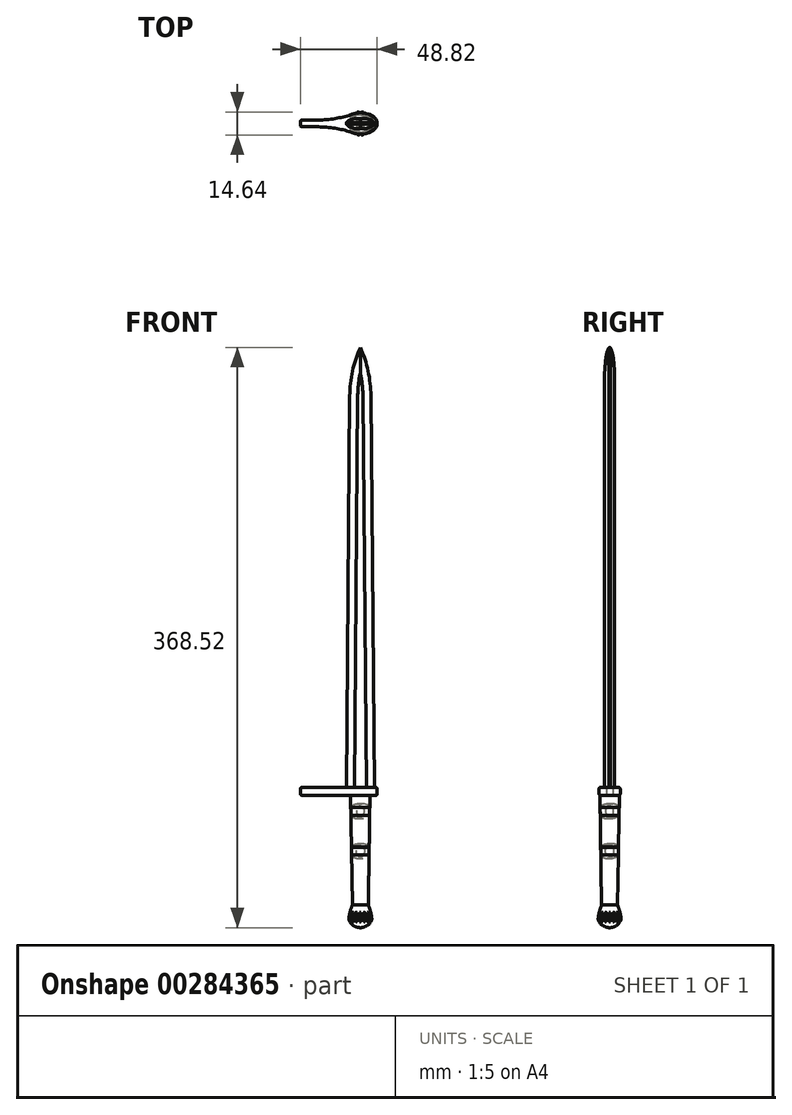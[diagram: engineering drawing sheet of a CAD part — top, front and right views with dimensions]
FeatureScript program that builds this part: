
annotation { "Feature Type Name" : "Feature", "Feature Type Description" : "" }
export const myFeature = defineFeature(function(context is Context, id is Id, definition is map)
    precondition{}
    {
        {
            var Q0;
            Q0=qCreatedBy(makeId("Right.planeOp"),FACE);
            var sketch = newSketch(context, id + "F0", { "sketchPlane" : qUnion([Q0])});
            skLineSegment(sketch, "E0", {"start": v(0, 0) * mm, "end": v(-6.1, 0) * mm});
            skLineSegment(sketch, "E1", {"start": v(0, 0) * mm, "end": v(0, -52.88) * mm});
            skLineSegment(sketch, "E2", {"start": v(0, 0) * mm, "end": v(6.1, 0) * mm});
            skPoint(sketch, "E3.end.orphan", {"position": v(-6.1, 0) * mm});
            skLineSegment(sketch, "E4", {"start": v(0, -52.88) * mm, "end": v(0, -69.72) * mm});
            skLineSegment(sketch, "E5", {"start": v(0, -69.72) * mm, "end": v(-5.08, -69.72) * mm});
            skLineSegment(sketch, "E6.MirrorCS", {"start": v(0, -69.72) * mm, "end": v(5.08, -69.72) * mm});
            skLineSegment(sketch, "E7", {"start": v(-5.08, -69.72) * mm, "end": v(-6.1, 0) * mm});
            skLineSegment(sketch, "E8", {"start": v(5.08, -69.72) * mm, "end": v(6.1, 0) * mm});
            skArc(sketch, "E9", {"start": v(-5.98, -7.62) * mm, "mid": v(-6.68, -10.11) * mm, "end": v(-5.91, -12.59) * mm});
            skLineSegment(sketch, "E10", {"start": v(-5.58, -35.4) * mm, "end": v(-13.44, -35.51) * mm});
            skArc(sketch, "E11.MirrorCS", {"start": v(-5.18, -63.18) * mm, "mid": v(-5.94, -60.7) * mm, "end": v(-5.25, -58.2) * mm});
            skLineSegment(sketch, "E12", {"start": v(-2.07, -10.05) * mm, "end": v(-5.91, -10.1) * mm});
            skLineSegment(sketch, "E13", {"start": v(-5.75, -22.75) * mm, "end": v(-5.91, -10.1) * mm});
            skPoint(sketch, "E14", {"position": v(-5.75, -22.75) * mm});
            skLineSegment(sketch, "E15", {"start": v(-5.75, -22.75) * mm, "end": v(-9.83, -22.8) * mm});
            skArc(sketch, "E16.MirrorCS", {"start": v(-5.59, -37.88) * mm, "mid": v(-6.34, -35.4) * mm, "end": v(-5.65, -32.91) * mm});
            skLineSegment(sketch, "E17", {"start": v(-5.59, -37.88) * mm, "end": v(-5.54, -37.95) * mm});
            skLineSegment(sketch, "E18", {"start": v(-5.65, -32.91) * mm, "end": v(-5.62, -32.87) * mm});
            skSolve(sketch);
        }
        {
            var Q0;
            {var subQ8=sQuery(id+"F0.wireOp",EDGE,"E0");Q0=makeQuery(id+"F0.imprint","IMPRINT",FACE,{"disambiguationData":[TD([[makeQuery(id+"F0.imprint","IMPRINT",EDGE,{"derivedFrom":subQ8}),1.0]])]});}
            var Q1;
            Q1=sQuery(id+"F0.wireOp",EDGE,"E1");
            revolve(context, id + "F1", {"entities" : qUnion([Q0]), "axis" : qUnion([Q1]), "revolveType" : RevolveType.FULL});
        }
        {
            var Q0;
            {var subQ3=sQuery(id+"F0.wireOp",EDGE,"E18");Q0=makeQuery(id+"F0.imprint","IMPRINT",FACE,{"disambiguationData":[TD([[makeQuery(id+"F0.imprint","IMPRINT",EDGE,{"derivedFrom":subQ3}),-1.0]])]});}
            var Q1;
            {var subQ3=sQuery(id+"F0.wireOp",EDGE,"E17");Q1=makeQuery(id+"F0.imprint","IMPRINT",FACE,{"disambiguationData":[TD([[makeQuery(id+"F0.imprint","IMPRINT",EDGE,{"derivedFrom":subQ3}),1.0]])]});}
            var Q2;
            {var subQ0=sQuery(id+"F0.wireOp",EDGE,"E9");Q2=makeQuery(id+"F0.imprint","IMPRINT",FACE,{"disambiguationData":[TD([[makeQuery(id+"F0.imprint","IMPRINT",EDGE,{"derivedFrom":subQ0}),1.0]])]});}
            var Q3;
            {var subQ0=sQuery(id+"F0.wireOp",EDGE,"E11.MirrorCS");Q3=makeQuery(id+"F0.imprint","IMPRINT",FACE,{"disambiguationData":[TD([[makeQuery(id+"F0.imprint","IMPRINT",EDGE,{"derivedFrom":subQ0}),-1.0]])]});}
            var Q4;
            Q4=sQuery(id+"F0.wireOp",EDGE,"E4");
            revolve(context, id + "F2", {"entities" : qUnion([Q0, Q1, Q2, Q3]), "axis" : qUnion([Q4]), "revolveType" : RevolveType.FULL});
        }
        {
            var Q0;
            Q0=makeQuery(id+"F1.opRevolve","SWEPT_FACE",FACE,{"disambiguationData":[OSD([sQuery(id+"F0.wireOp",EDGE,"E0")])]});
            var sketch = newSketch(context, id + "F3", { "sketchPlane" : qUnion([Q0])});
            skEllipse(sketch, "E19", {"center": v(0, 0) * mm, "majorRadius": 6.74 * mm, "minorRadius": 10.7 * mm, "majorAxis": v(0, 1)});
            skLineSegment(sketch, "E20", {"start": v(-10.7, 0) * mm, "end": v(-38.12, 0) * mm});
            skPoint(sketch, "E20.endSnap0", {"position": v(-10.7, 0) * mm});
            skLineSegment(sketch, "E21", {"start": v(-38.12, 0) * mm, "end": v(-38.12, 2.16) * mm});
            skLineSegment(sketch, "E22", {"start": v(-38.12, 2.16) * mm, "end": v(-27.96, 2.16) * mm});
            skArc(sketch, "E23", {"start": v(-27.96, 2.16) * mm, "mid": v(-17.38, 2.9) * mm, "end": v(-7, 5.1) * mm});
            skArc(sketch, "E24.MirrorCS", {"start": v(-27.96, -2.16) * mm, "mid": v(-17.38, -2.9) * mm, "end": v(-7, -5.1) * mm});
            skLineSegment(sketch, "E25.MirrorCS", {"start": v(-38.12, -2.16) * mm, "end": v(-27.96, -2.16) * mm});
            skLineSegment(sketch, "E26.MirrorCS", {"start": v(-38.12, 0) * mm, "end": v(-38.12, -2.16) * mm});
            skLineSegment(sketch, "E27", {"start": v(0, 0) * mm, "end": v(0, 3.03) * mm});
            skArc(sketch, "E28.MirrorCS", {"start": v(27.96, 2.16) * mm, "mid": v(17.38, 2.9) * mm, "end": v(7, 5.1) * mm});
            skArc(sketch, "E29.MirrorCS", {"start": v(27.96, -2.16) * mm, "mid": v(17.38, -2.9) * mm, "end": v(7, -5.1) * mm});
            skLineSegment(sketch, "E30.MirrorCS", {"start": v(38.12, 0) * mm, "end": v(38.12, -2.16) * mm});
            skLineSegment(sketch, "E31.MirrorCS", {"start": v(38.12, 0) * mm, "end": v(38.12, 2.16) * mm});
            skLineSegment(sketch, "E32.MirrorCS", {"start": v(38.12, 2.16) * mm, "end": v(27.96, 2.16) * mm});
            skLineSegment(sketch, "E33.MirrorCS", {"start": v(38.12, -2.16) * mm, "end": v(27.96, -2.16) * mm});
            skSolve(sketch);
        }
        {
            var Q0;
            {var subQ1=sQuery(id+"F3.wireOp",EDGE,"E20");Q0=makeQuery(id+"F3.imprint","IMPRINT",FACE,{"disambiguationData":[TD([[makeQuery(id+"F3.imprint","IMPRINT",EDGE,{"derivedFrom":subQ1}),-1.0]])]});}
            var Q1;
            {var subQ1=sQuery(id+"F3.wireOp",EDGE,"E20");Q1=makeQuery(id+"F3.imprint","IMPRINT",FACE,{"disambiguationData":[TD([[makeQuery(id+"F3.imprint","IMPRINT",EDGE,{"derivedFrom":subQ1}),1.0]])]});}
            var Q2;
            Q2=makeQuery(id+"F3.imprint","IMPRINT",FACE,{"disambiguationData":[TD([[makeQuery(id+"F3.imprint","IMPRINT",EDGE,{"derivedFrom":makeQuery(id+"F1.opRevolve","SWEPT_EDGE",EDGE,{"disambiguationData":[OSD([sQuery(id+"F0.wireOp",EDGE,"E0"),sQuery(id+"F0.wireOp",EDGE,"E7")])]})}),-1.0]])]});
            var Q3;
            {var subQ0=sQuery(id+"F3.wireOp",EDGE,"E28.MirrorCS");Q3=makeQuery(id+"F3.imprint","IMPRINT",FACE,{"disambiguationData":[TD([[makeQuery(id+"F3.imprint","IMPRINT",EDGE,{"derivedFrom":subQ0}),1.0]])]});}
            var Q4;
            Q4=makeQuery(id+"F3.imprint","IMPRINT",FACE,{"disambiguationData":[TD([[makeQuery(id+"F3.imprint","IMPRINT",EDGE,{"derivedFrom":makeQuery(id+"F1.opRevolve","SWEPT_EDGE",EDGE,{"disambiguationData":[OSD([sQuery(id+"F0.wireOp",EDGE,"E0"),sQuery(id+"F0.wireOp",EDGE,"E7")])]})}),1.0]])]});
            extrude(context, id + "F4", {"entities" : qUnion([Q0, Q1, Q2, Q3, Q4]), "depth" : 5.08 * mm});
        }
        {
            var Q0;
            Q0=makeQuery(id+"F4.opExtrude","CAP_EDGE",EDGE,{"disambiguationData":[OSD([sQuery(id+"F3.wireOp",EDGE,"E24.MirrorCS")])],"isStart":false});
            var Q1;
            Q1=makeQuery(id+"F4.opExtrude","CAP_EDGE",EDGE,{"disambiguationData":[OSD([sQuery(id+"F3.wireOp",EDGE,"E25.MirrorCS")])],"isStart":false});
            var Q2;
            Q2=makeQuery(id+"F4.opExtrude","CAP_EDGE",EDGE,{"disambiguationData":[OSD([sQuery(id+"F3.wireOp",EDGE,"E25.MirrorCS")])],"isStart":true});
            var Q3;
            Q3=makeQuery(id+"F4.opExtrude","CAP_EDGE",EDGE,{"disambiguationData":[OSD([sQuery(id+"F3.wireOp",EDGE,"E24.MirrorCS")])],"isStart":true});
            var Q4;
            Q4=makeQuery(id+"F4.opExtrude","CAP_EDGE",EDGE,{"disambiguationData":[OSD([sQuery(id+"F3.wireOp",EDGE,"E23")])],"isStart":true});
            var Q5;
            Q5=makeQuery(id+"F4.opExtrude","CAP_EDGE",EDGE,{"disambiguationData":[OSD([sQuery(id+"F3.wireOp",EDGE,"E23")])],"isStart":false});
            var Q6;
            Q6=makeQuery(id+"F4.opExtrude","CAP_EDGE",EDGE,{"disambiguationData":[OSD([sQuery(id+"F3.wireOp",EDGE,"E22")])],"isStart":false});
            var Q7;
            Q7=makeQuery(id+"F4.opExtrude","SWEPT_EDGE",EDGE,{"disambiguationData":[OSD([sQuery(id+"F3.wireOp",EDGE,"E25.MirrorCS"),sQuery(id+"F3.wireOp",EDGE,"E26.MirrorCS")])]});
            var Q8;
            Q8=makeQuery(id+"F4.opExtrude","SWEPT_EDGE",EDGE,{"disambiguationData":[OSD([sQuery(id+"F3.wireOp",EDGE,"E21"),sQuery(id+"F3.wireOp",EDGE,"E22")])]});
            var Q9;
            Q9=makeQuery(id+"F4.opExtrude","CAP_EDGE",EDGE,{"disambiguationData":[OSD([sQuery(id+"F3.wireOp",EDGE,"E21"),sQuery(id+"F3.wireOp",EDGE,"E26.MirrorCS")])],"isStart":true});
            var Q10;
            Q10=makeQuery(id+"F4.opExtrude","CAP_EDGE",EDGE,{"disambiguationData":[OSD([sQuery(id+"F3.wireOp",EDGE,"E21"),sQuery(id+"F3.wireOp",EDGE,"E26.MirrorCS")])],"isStart":false});
            var Q11;
            Q11=makeQuery(id+"F4.opExtrude","CAP_EDGE",EDGE,{"disambiguationData":[OSD([sQuery(id+"F3.wireOp",EDGE,"E29.MirrorCS")])],"isStart":false});
            var Q12;
            Q12=makeQuery(id+"F4.opExtrude","CAP_EDGE",EDGE,{"disambiguationData":[OSD([sQuery(id+"F3.wireOp",EDGE,"E29.MirrorCS")])],"isStart":true});
            var Q13;
            Q13=makeQuery(id+"F4.opExtrude","CAP_EDGE",EDGE,{"disambiguationData":[OSD([sQuery(id+"F3.wireOp",EDGE,"E28.MirrorCS")])],"isStart":false});
            var Q14;
            Q14=makeQuery(id+"F4.opExtrude","CAP_EDGE",EDGE,{"disambiguationData":[OSD([sQuery(id+"F3.wireOp",EDGE,"E28.MirrorCS")])],"isStart":true});
            var Q15;
            Q15=makeQuery(id+"F4.opExtrude","SWEPT_FACE",FACE,{"disambiguationData":[OSD([sQuery(id+"F3.wireOp",EDGE,"E30.MirrorCS"),sQuery(id+"F3.wireOp",EDGE,"E31.MirrorCS")])]});
            var Q16;
            {var subQ0=sQuery(id+"F3.wireOp",EDGE,"E19");Q16=makeQuery(id+"F4.opExtrude","SWEPT_FACE",FACE,{"disambiguationData":[OSD([subQ0]),TDD([makeQuery(id+"F3.imprint","IMPRINT",EDGE,{"disambiguationData":[TD([[makeQuery(id+"F3.imprint","INTERSECT",VERTEX,{"derivedFrom":[subQ0,sQuery(id+"F3.wireOp",EDGE,"E24.MirrorCS")]}),-1.0]])],"derivedFrom":subQ0})])]});}
            var Q17;
            {var subQ0=sQuery(id+"F3.wireOp",EDGE,"E19");Q17=makeQuery(id+"F4.opExtrude","SWEPT_FACE",FACE,{"disambiguationData":[OSD([subQ0]),TDD([makeQuery(id+"F3.imprint","IMPRINT",EDGE,{"disambiguationData":[TD([[makeQuery(id+"F3.imprint","INTERSECT",VERTEX,{"derivedFrom":[subQ0,sQuery(id+"F3.wireOp",EDGE,"E23")]}),1.0]])],"derivedFrom":subQ0})])]});}
            fillet(context, id + "F5", {"entities" : qUnion([Q0, Q1, Q2, Q3, Q4, Q5, Q6, Q7, Q8, Q9, Q10, Q11, Q12, Q13, Q14, Q15, Q16, Q17]), "radius" : 1.02 * mm, "tangentPropagation" : true, "allowEdgeOverflow" : false});
        }
        {
            var Q0;
            Q0=qCreatedBy(makeId("Front.planeOp"),FACE);
            var sketch = newSketch(context, id + "F6", { "sketchPlane" : qUnion([Q0])});
            skLineSegment(sketch, "E34.0", {"start": v(-5.08, -69.72) * mm, "end": v(5.08, -69.72) * mm});
            skArc(sketch, "E35", {"start": v(-5.08, -69.72) * mm, "mid": v(-6.56, -74.06) * mm, "end": v(-7.37, -78.58) * mm});
            skLineSegment(sketch, "E36", {"start": v(0, -69.72) * mm, "end": v(0, -75.64) * mm});
            skPoint(sketch, "E36.endSnap0", {"position": v(0, -69.72) * mm});
            skArc(sketch, "E37.MirrorCS", {"start": v(5.08, -69.72) * mm, "mid": v(6.56, -74.06) * mm, "end": v(7.37, -78.58) * mm});
            skArc(sketch, "E38", {"start": v(-7.37, -78.58) * mm, "mid": v(0, -84.04) * mm, "end": v(7.37, -78.58) * mm});
            skLineSegment(sketch, "E39", {"start": v(0, -72.68) * mm, "end": v(0, -84.04) * mm});
            skSolve(sketch);
        }
        {
            var Q0;
            {var subQ1=sQuery(id+"F6.wireOp",EDGE,"E35");Q0=makeQuery(id+"F6.imprint","IMPRINT",FACE,{"disambiguationData":[TD([[makeQuery(id+"F6.imprint","IMPRINT",EDGE,{"derivedFrom":subQ1}),1.0]])]});}
            var Q1;
            Q1=sQuery(id+"F6.wireOp",EDGE,"E39");
            revolve(context, id + "F7", {"entities" : qUnion([Q0]), "axis" : qUnion([Q1]), "revolveType" : RevolveType.FULL});
        }
        {
            var Q0;
            Q0=makeQuery(id+"F7.opRevolve","SWEPT_FACE",FACE,{"disambiguationData":[OSD([sQuery(id+"F6.wireOp",EDGE,"E34.0")])]});
            var sketch = newSketch(context, id + "F8", { "sketchPlane" : qUnion([Q0])});
            skCircle(sketch, "E40.0", {"center": v(0, 0) * mm, "radius": 7.37 * mm});
            skLineSegment(sketch, "E41", {"start": v(-0.9, 7.32) * mm, "end": v(-0.35, 6.6) * mm});
            skLineSegment(sketch, "E42", {"start": v(0, 7.32) * mm, "end": v(0, 7.11) * mm});
            skLineSegment(sketch, "E43.MirrorCS", {"start": v(0.9, 7.32) * mm, "end": v(0.35, 6.6) * mm});
            skLineSegment(sketch, "E44", {"start": v(-0.35, 6.6) * mm, "end": v(0.35, 6.6) * mm});
            skPoint(sketch, "E45.orphan", {"position": v(0.9, 7.32) * mm});
            skLineSegment(sketch, "E46.1.0", {"start": v(-1.97, 7.1) * mm, "end": v(-2.2, 6.23) * mm});
            skLineSegment(sketch, "E46.1.1", {"start": v(-2.85, 5.96) * mm, "end": v(-2.2, 6.23) * mm});
            skLineSegment(sketch, "E46.1.2", {"start": v(-3.63, 6.42) * mm, "end": v(-2.85, 5.96) * mm});
            skLineSegment(sketch, "E46.2.0", {"start": v(-4.54, 5.8) * mm, "end": v(-4.42, 4.92) * mm});
            skLineSegment(sketch, "E46.2.1", {"start": v(-4.92, 4.42) * mm, "end": v(-4.42, 4.92) * mm});
            skLineSegment(sketch, "E46.2.2", {"start": v(-5.8, 4.54) * mm, "end": v(-4.92, 4.42) * mm});
            skLineSegment(sketch, "E46.3.0", {"start": v(-6.42, 3.63) * mm, "end": v(-5.96, 2.85) * mm});
            skLineSegment(sketch, "E46.3.1", {"start": v(-6.23, 2.2) * mm, "end": v(-5.96, 2.85) * mm});
            skLineSegment(sketch, "E46.3.2", {"start": v(-7.1, 1.97) * mm, "end": v(-6.23, 2.2) * mm});
            skLineSegment(sketch, "E46.4.0", {"start": v(-7.32, 0.9) * mm, "end": v(-6.6, 0.35) * mm});
            skLineSegment(sketch, "E46.4.1", {"start": v(-6.6, -0.35) * mm, "end": v(-6.6, 0.35) * mm});
            skLineSegment(sketch, "E46.4.2", {"start": v(-7.32, -0.9) * mm, "end": v(-6.6, -0.35) * mm});
            skLineSegment(sketch, "E46.5.0", {"start": v(-7.1, -1.97) * mm, "end": v(-6.23, -2.2) * mm});
            skLineSegment(sketch, "E46.5.1", {"start": v(-5.96, -2.85) * mm, "end": v(-6.23, -2.2) * mm});
            skLineSegment(sketch, "E46.5.2", {"start": v(-6.42, -3.63) * mm, "end": v(-5.96, -2.85) * mm});
            skLineSegment(sketch, "E46.6.0", {"start": v(-5.8, -4.54) * mm, "end": v(-4.92, -4.42) * mm});
            skLineSegment(sketch, "E46.6.1", {"start": v(-4.42, -4.92) * mm, "end": v(-4.92, -4.42) * mm});
            skLineSegment(sketch, "E46.6.2", {"start": v(-4.54, -5.8) * mm, "end": v(-4.42, -4.92) * mm});
            skLineSegment(sketch, "E46.7.0", {"start": v(-3.63, -6.42) * mm, "end": v(-2.85, -5.96) * mm});
            skLineSegment(sketch, "E46.7.1", {"start": v(-2.2, -6.23) * mm, "end": v(-2.85, -5.96) * mm});
            skLineSegment(sketch, "E46.7.2", {"start": v(-1.97, -7.1) * mm, "end": v(-2.2, -6.23) * mm});
            skLineSegment(sketch, "E46.8.0", {"start": v(-0.9, -7.32) * mm, "end": v(-0.35, -6.6) * mm});
            skLineSegment(sketch, "E46.8.1", {"start": v(0.35, -6.6) * mm, "end": v(-0.35, -6.6) * mm});
            skLineSegment(sketch, "E46.8.2", {"start": v(0.9, -7.32) * mm, "end": v(0.35, -6.6) * mm});
            skLineSegment(sketch, "E46.9.0", {"start": v(1.97, -7.1) * mm, "end": v(2.2, -6.23) * mm});
            skLineSegment(sketch, "E46.9.1", {"start": v(2.85, -5.96) * mm, "end": v(2.2, -6.23) * mm});
            skLineSegment(sketch, "E46.9.2", {"start": v(3.63, -6.42) * mm, "end": v(2.85, -5.96) * mm});
            skLineSegment(sketch, "E46.10.0", {"start": v(4.54, -5.8) * mm, "end": v(4.42, -4.92) * mm});
            skLineSegment(sketch, "E46.10.1", {"start": v(4.92, -4.42) * mm, "end": v(4.42, -4.92) * mm});
            skLineSegment(sketch, "E46.10.2", {"start": v(5.8, -4.54) * mm, "end": v(4.92, -4.42) * mm});
            skLineSegment(sketch, "E46.11.0", {"start": v(6.42, -3.63) * mm, "end": v(5.96, -2.85) * mm});
            skLineSegment(sketch, "E46.11.1", {"start": v(6.23, -2.2) * mm, "end": v(5.96, -2.85) * mm});
            skLineSegment(sketch, "E46.11.2", {"start": v(7.1, -1.97) * mm, "end": v(6.23, -2.2) * mm});
            skLineSegment(sketch, "E46.12.0", {"start": v(7.32, -0.9) * mm, "end": v(6.6, -0.35) * mm});
            skLineSegment(sketch, "E46.12.1", {"start": v(6.6, 0.35) * mm, "end": v(6.6, -0.35) * mm});
            skLineSegment(sketch, "E46.12.2", {"start": v(7.32, 0.9) * mm, "end": v(6.6, 0.35) * mm});
            skLineSegment(sketch, "E46.13.0", {"start": v(7.1, 1.97) * mm, "end": v(6.23, 2.2) * mm});
            skLineSegment(sketch, "E46.13.1", {"start": v(5.96, 2.85) * mm, "end": v(6.23, 2.2) * mm});
            skLineSegment(sketch, "E46.13.2", {"start": v(6.42, 3.63) * mm, "end": v(5.96, 2.85) * mm});
            skLineSegment(sketch, "E46.14.0", {"start": v(5.8, 4.54) * mm, "end": v(4.92, 4.42) * mm});
            skLineSegment(sketch, "E46.14.1", {"start": v(4.42, 4.92) * mm, "end": v(4.92, 4.42) * mm});
            skLineSegment(sketch, "E46.14.2", {"start": v(4.54, 5.8) * mm, "end": v(4.42, 4.92) * mm});
            skLineSegment(sketch, "E46.15.0", {"start": v(3.63, 6.42) * mm, "end": v(2.85, 5.96) * mm});
            skLineSegment(sketch, "E46.15.1", {"start": v(2.2, 6.23) * mm, "end": v(2.85, 5.96) * mm});
            skLineSegment(sketch, "E46.15.2", {"start": v(1.97, 7.1) * mm, "end": v(2.2, 6.23) * mm});
            skSolve(sketch);
        }
        {
            var Q0;
            {var subQ0=sQuery(id+"F8.wireOp",EDGE,"E46.3.0");Q0=makeQuery(id+"F8.imprint","IMPRINT",FACE,{"disambiguationData":[TD([[makeQuery(id+"F8.imprint","IMPRINT",EDGE,{"derivedFrom":subQ0}),-1.0]])]});}
            var Q1;
            {var subQ0=sQuery(id+"F8.wireOp",EDGE,"E46.4.0");Q1=makeQuery(id+"F8.imprint","IMPRINT",FACE,{"disambiguationData":[TD([[makeQuery(id+"F8.imprint","IMPRINT",EDGE,{"derivedFrom":subQ0}),-1.0]])]});}
            var Q2;
            {var subQ0=sQuery(id+"F8.wireOp",EDGE,"E46.5.0");Q2=makeQuery(id+"F8.imprint","IMPRINT",FACE,{"disambiguationData":[TD([[makeQuery(id+"F8.imprint","IMPRINT",EDGE,{"derivedFrom":subQ0}),-1.0]])]});}
            var Q3;
            {var subQ0=sQuery(id+"F8.wireOp",EDGE,"E46.6.0");Q3=makeQuery(id+"F8.imprint","IMPRINT",FACE,{"disambiguationData":[TD([[makeQuery(id+"F8.imprint","IMPRINT",EDGE,{"derivedFrom":subQ0}),-1.0]])]});}
            var Q4;
            {var subQ0=sQuery(id+"F8.wireOp",EDGE,"E46.7.0");Q4=makeQuery(id+"F8.imprint","IMPRINT",FACE,{"disambiguationData":[TD([[makeQuery(id+"F8.imprint","IMPRINT",EDGE,{"derivedFrom":subQ0}),-1.0]])]});}
            var Q5;
            {var subQ0=sQuery(id+"F8.wireOp",EDGE,"E46.8.0");Q5=makeQuery(id+"F8.imprint","IMPRINT",FACE,{"disambiguationData":[TD([[makeQuery(id+"F8.imprint","IMPRINT",EDGE,{"derivedFrom":subQ0}),-1.0]])]});}
            var Q6;
            {var subQ0=sQuery(id+"F8.wireOp",EDGE,"E46.9.0");Q6=makeQuery(id+"F8.imprint","IMPRINT",FACE,{"disambiguationData":[TD([[makeQuery(id+"F8.imprint","IMPRINT",EDGE,{"derivedFrom":subQ0}),-1.0]])]});}
            var Q7;
            {var subQ0=sQuery(id+"F8.wireOp",EDGE,"E46.10.0");Q7=makeQuery(id+"F8.imprint","IMPRINT",FACE,{"disambiguationData":[TD([[makeQuery(id+"F8.imprint","IMPRINT",EDGE,{"derivedFrom":subQ0}),-1.0]])]});}
            var Q8;
            {var subQ0=sQuery(id+"F8.wireOp",EDGE,"E46.11.0");Q8=makeQuery(id+"F8.imprint","IMPRINT",FACE,{"disambiguationData":[TD([[makeQuery(id+"F8.imprint","IMPRINT",EDGE,{"derivedFrom":subQ0}),-1.0]])]});}
            var Q9;
            {var subQ0=sQuery(id+"F8.wireOp",EDGE,"E46.12.0");Q9=makeQuery(id+"F8.imprint","IMPRINT",FACE,{"disambiguationData":[TD([[makeQuery(id+"F8.imprint","IMPRINT",EDGE,{"derivedFrom":subQ0}),-1.0]])]});}
            var Q10;
            {var subQ0=sQuery(id+"F8.wireOp",EDGE,"E46.13.0");Q10=makeQuery(id+"F8.imprint","IMPRINT",FACE,{"disambiguationData":[TD([[makeQuery(id+"F8.imprint","IMPRINT",EDGE,{"derivedFrom":subQ0}),-1.0]])]});}
            var Q11;
            {var subQ0=sQuery(id+"F8.wireOp",EDGE,"E46.14.0");Q11=makeQuery(id+"F8.imprint","IMPRINT",FACE,{"disambiguationData":[TD([[makeQuery(id+"F8.imprint","IMPRINT",EDGE,{"derivedFrom":subQ0}),-1.0]])]});}
            var Q12;
            {var subQ0=sQuery(id+"F8.wireOp",EDGE,"E46.15.0");Q12=makeQuery(id+"F8.imprint","IMPRINT",FACE,{"disambiguationData":[TD([[makeQuery(id+"F8.imprint","IMPRINT",EDGE,{"derivedFrom":subQ0}),-1.0]])]});}
            var Q13;
            {var subQ0=sQuery(id+"F8.wireOp",EDGE,"E41");Q13=makeQuery(id+"F8.imprint","IMPRINT",FACE,{"disambiguationData":[TD([[makeQuery(id+"F8.imprint","IMPRINT",EDGE,{"derivedFrom":subQ0}),1.0]])]});}
            var Q14;
            {var subQ0=sQuery(id+"F8.wireOp",EDGE,"E46.1.0");Q14=makeQuery(id+"F8.imprint","IMPRINT",FACE,{"disambiguationData":[TD([[makeQuery(id+"F8.imprint","IMPRINT",EDGE,{"derivedFrom":subQ0}),-1.0]])]});}
            var Q15;
            {var subQ0=sQuery(id+"F8.wireOp",EDGE,"E46.2.0");Q15=makeQuery(id+"F8.imprint","IMPRINT",FACE,{"disambiguationData":[TD([[makeQuery(id+"F8.imprint","IMPRINT",EDGE,{"derivedFrom":subQ0}),-1.0]])]});}
            extrude(context, id + "F9", {"entities" : qUnion([Q0, Q1, Q2, Q3, Q4, Q5, Q6, Q7, Q8, Q9, Q10, Q11, Q12, Q13, Q14, Q15]), "operationType" : NewBodyOperationType.REMOVE, "oppositeDirection" : true, "depth" : 25.4 * mm});
        }
        {
            var Q0;
            Q0=qCreatedBy(makeId("Front.planeOp"),FACE);
            var sketch = newSketch(context, id + "F10", { "sketchPlane" : qUnion([Q0])});
            skFitSpline(sketch, "E47.0", {"points": [v(-6.43, 5.08) * mm, v(-2.14, 5.08) * mm, v(2.14, 5.08) * mm, v(6.43, 5.08) * mm]});
            skLineSegment(sketch, "E48.0", {"start": v(-6.43, 5.08) * mm, "end": v(-6.83, 5.08) * mm});
            skLineSegment(sketch, "E49.0", {"start": v(-27.96, 5.08) * mm, "end": v(-6.83, 5.08) * mm});
            skLineSegment(sketch, "E50.0", {"start": v(6.83, 5.08) * mm, "end": v(27.96, 5.08) * mm});
            skLineSegment(sketch, "E51.0", {"start": v(6.83, 5.08) * mm, "end": v(6.43, 5.08) * mm});
            skArc(sketch, "E52", {"start": v(-6.6, -80.31) * mm, "mid": v(0, -84.04) * mm, "end": v(6.6, -80.31) * mm});
            skPoint(sketch, "E53", {"position": v(0, 5.08) * mm});
            skPoint(sketch, "E54", {"position": v(0, -84.04) * mm});
            skLineSegment(sketch, "E55", {"start": v(0, 5.08) * mm, "end": v(0, 284.48) * mm});
            skPoint(sketch, "E56", {"position": v(-8.9, 5.08) * mm});
            skLineSegment(sketch, "E57", {"start": v(-8.9, 5.08) * mm, "end": v(-6.72, 253.77) * mm});
            skLineSegment(sketch, "E58", {"start": v(-6.83, 5.08) * mm, "end": v(-8.9, 5.08) * mm});
            skArc(sketch, "E59", {"start": v(0, 284.48) * mm, "mid": v(-4.95, 269.47) * mm, "end": v(-6.72, 253.77) * mm});
            skLineSegment(sketch, "E60.MirrorCS", {"start": v(8.9, 5.08) * mm, "end": v(6.72, 253.77) * mm});
            skArc(sketch, "E61.MirrorCS", {"start": v(0, 284.48) * mm, "mid": v(4.95, 269.47) * mm, "end": v(6.72, 253.77) * mm});
            skSolve(sketch);
        }
        {
            var Q0;
            Q0=qSketchRegion(id+"F10",true);
            extrude(context, id + "F11", {"entities" : qUnion([Q0]), "endBound" : BoundingType.SYMMETRIC, "depth" : 6.35 * mm});
        }
        {
            var Q0;
            Q0=makeQuery(id+"F11.opExtrude","CAP_EDGE",EDGE,{"disambiguationData":[OSD([sQuery(id+"F10.wireOp",EDGE,"E57")])],"isStart":false});
            var Q1;
            Q1=makeQuery(id+"F11.opExtrude","CAP_EDGE",EDGE,{"disambiguationData":[OSD([sQuery(id+"F10.wireOp",EDGE,"E60.MirrorCS")])],"isStart":false});
            chamfer(context, id + "F12", {"entities" : qUnion([Q0, Q1]), "chamferType" : ChamferType.TWO_OFFSETS, "width1" : 1.52 * mm, "oppositeDirection" : false, "width2" : 5.08 * mm, "tangentPropagation" : true});
        }
        {
            var Q0;
            Q0=makeQuery(id+"F11.opExtrude","CAP_EDGE",EDGE,{"disambiguationData":[OSD([sQuery(id+"F10.wireOp",EDGE,"E60.MirrorCS")])],"isStart":true});
            var Q1;
            Q1=makeQuery(id+"F11.opExtrude","CAP_EDGE",EDGE,{"disambiguationData":[OSD([sQuery(id+"F10.wireOp",EDGE,"E57")])],"isStart":true});
            chamfer(context, id + "F13", {"entities" : qUnion([Q0, Q1]), "chamferType" : ChamferType.TWO_OFFSETS, "width1" : 1.52 * mm, "oppositeDirection" : false, "width2" : 5.08 * mm, "tangentPropagation" : true});
        }
        {
            var Q0;
            Q0=qCreatedBy(makeId("Front.planeOp"),FACE);
            var sketch = newSketch(context, id + "F14", { "sketchPlane" : qUnion([Q0])});
            skLineSegment(sketch, "E62.0", {"start": v(-3.8, 5.08) * mm, "end": v(-6.43, 5.08) * mm});
            skFitSpline(sketch, "E63.0", {"points": [v(-6.43, 5.08) * mm, v(-2.14, 5.08) * mm, v(2.14, 5.08) * mm, v(6.43, 5.08) * mm]});
            skLineSegment(sketch, "E64.0", {"start": v(6.43, 5.08) * mm, "end": v(3.8, 5.08) * mm});
            skLineSegment(sketch, "E65", {"start": v(-5.55, 5.08) * mm, "end": v(-3.57, -75.16) * mm});
            skLineSegment(sketch, "E66", {"start": v(0, 5.08) * mm, "end": v(0, -77.77) * mm});
            skLineSegment(sketch, "E67.MirrorCS", {"start": v(5.55, 5.08) * mm, "end": v(3.57, -75.16) * mm});
            skLineSegment(sketch, "E68", {"start": v(-3.57, -75.16) * mm, "end": v(3.57, -75.16) * mm});
            skSolve(sketch);
        }
        {
            var Q0;
            Q0=qSketchRegion(id+"F14",true);
            extrude(context, id + "F15", {"entities" : qUnion([Q0]), "operationType" : NewBodyOperationType.REMOVE, "endBound" : BoundingType.SYMMETRIC, "oppositeDirection" : true, "depth" : 2.03 * mm});
        }
        {
            var Q0;
            {var subQ5=sQuery(id+"F14.wireOp",EDGE,"E65");Q0=makeQuery(id+"F14.imprint","IMPRINT",FACE,{"disambiguationData":[TD([[makeQuery(id+"F14.imprint","IMPRINT",EDGE,{"derivedFrom":subQ5}),1.0]])]});}
            var Q1;
            {var subQ7=sQuery(id+"F14.wireOp",EDGE,"E67.MirrorCS");Q1=makeQuery(id+"F14.imprint","IMPRINT",FACE,{"disambiguationData":[TD([[makeQuery(id+"F14.imprint","IMPRINT",EDGE,{"derivedFrom":subQ7}),-1.0]])]});}
            extrude(context, id + "F16", {"entities" : qUnion([Q0, Q1]), "operationType" : NewBodyOperationType.ADD, "endBound" : BoundingType.SYMMETRIC, "depth" : 2.03 * mm});
        }
        {
            var Q0;
            {var subQ0=sQuery(id+"F10.wireOp",EDGE,"E57");Q0=makeQuery(id+"F13.opChamfer","BLEND_EDGE",EDGE,{"blendedFrom":[makeQuery(id+"F11.opExtrude","CAP_EDGE",EDGE,{"disambiguationData":[OSD([subQ0])],"isStart":true}),makeQuery(id+"F11.opExtrude","SWEPT_FACE",FACE,{"disambiguationData":[OSD([subQ0])]})],"blendedInto":[makeQuery(id+"F11.opExtrude","SWEPT_FACE",FACE,{"disambiguationData":[OSD([subQ0])]})]});}
            var Q1;
            {var subQ0=sQuery(id+"F10.wireOp",EDGE,"E57");Q1=makeQuery(id+"F12.opChamfer","BLEND_EDGE",EDGE,{"blendedFrom":[makeQuery(id+"F11.opExtrude","CAP_EDGE",EDGE,{"disambiguationData":[OSD([subQ0])],"isStart":false}),makeQuery(id+"F11.opExtrude","SWEPT_FACE",FACE,{"disambiguationData":[OSD([subQ0])]})],"blendedInto":[makeQuery(id+"F11.opExtrude","SWEPT_FACE",FACE,{"disambiguationData":[OSD([subQ0])]})]});}
            var Q2;
            {var subQ0=sQuery(id+"F10.wireOp",EDGE,"E59");Q2=makeQuery(id+"F12.opChamfer","BLEND_EDGE",EDGE,{"blendedFrom":[makeQuery(id+"F11.opExtrude","CAP_EDGE",EDGE,{"disambiguationData":[OSD([subQ0])],"isStart":false}),makeQuery(id+"F11.opExtrude","SWEPT_FACE",FACE,{"disambiguationData":[OSD([subQ0])]})],"blendedInto":[makeQuery(id+"F11.opExtrude","SWEPT_FACE",FACE,{"disambiguationData":[OSD([subQ0])]})]});}
            var Q3;
            {var subQ0=sQuery(id+"F10.wireOp",EDGE,"E59");Q3=makeQuery(id+"F13.opChamfer","BLEND_EDGE",EDGE,{"blendedFrom":[makeQuery(id+"F11.opExtrude","CAP_EDGE",EDGE,{"disambiguationData":[OSD([subQ0])],"isStart":true}),makeQuery(id+"F11.opExtrude","SWEPT_FACE",FACE,{"disambiguationData":[OSD([subQ0])]})],"blendedInto":[makeQuery(id+"F11.opExtrude","SWEPT_FACE",FACE,{"disambiguationData":[OSD([subQ0])]})]});}
            var Q4;
            {var subQ0=sQuery(id+"F10.wireOp",EDGE,"E61.MirrorCS");Q4=makeQuery(id+"F13.opChamfer","BLEND_EDGE",EDGE,{"blendedFrom":[makeQuery(id+"F11.opExtrude","CAP_EDGE",EDGE,{"disambiguationData":[OSD([subQ0])],"isStart":true}),makeQuery(id+"F11.opExtrude","SWEPT_FACE",FACE,{"disambiguationData":[OSD([subQ0])]})],"blendedInto":[makeQuery(id+"F11.opExtrude","SWEPT_FACE",FACE,{"disambiguationData":[OSD([subQ0])]})]});}
            var Q5;
            {var subQ0=sQuery(id+"F10.wireOp",EDGE,"E61.MirrorCS");Q5=makeQuery(id+"F12.opChamfer","BLEND_EDGE",EDGE,{"blendedFrom":[makeQuery(id+"F11.opExtrude","CAP_EDGE",EDGE,{"disambiguationData":[OSD([subQ0])],"isStart":false}),makeQuery(id+"F11.opExtrude","SWEPT_FACE",FACE,{"disambiguationData":[OSD([subQ0])]})],"blendedInto":[makeQuery(id+"F11.opExtrude","SWEPT_FACE",FACE,{"disambiguationData":[OSD([subQ0])]})]});}
            var Q6;
            {var subQ0=sQuery(id+"F10.wireOp",EDGE,"E60.MirrorCS");Q6=makeQuery(id+"F12.opChamfer","BLEND_EDGE",EDGE,{"blendedFrom":[makeQuery(id+"F11.opExtrude","CAP_EDGE",EDGE,{"disambiguationData":[OSD([subQ0])],"isStart":false}),makeQuery(id+"F11.opExtrude","SWEPT_FACE",FACE,{"disambiguationData":[OSD([subQ0])]})],"blendedInto":[makeQuery(id+"F11.opExtrude","SWEPT_FACE",FACE,{"disambiguationData":[OSD([subQ0])]})]});}
            var Q7;
            {var subQ0=sQuery(id+"F10.wireOp",EDGE,"E60.MirrorCS");Q7=makeQuery(id+"F13.opChamfer","BLEND_EDGE",EDGE,{"blendedFrom":[makeQuery(id+"F11.opExtrude","CAP_EDGE",EDGE,{"disambiguationData":[OSD([subQ0])],"isStart":true}),makeQuery(id+"F11.opExtrude","SWEPT_FACE",FACE,{"disambiguationData":[OSD([subQ0])]})],"blendedInto":[makeQuery(id+"F11.opExtrude","SWEPT_FACE",FACE,{"disambiguationData":[OSD([subQ0])]})]});}
            chamfer(context, id + "F17", {"entities" : qUnion([Q0, Q1, Q2, Q3, Q4, Q5, Q6, Q7]), "width" : 1.65 * mm, "tangentPropagation" : true});
        }
        {
            var Q0;
            {var subQ0=sQuery(id+"F10.wireOp",EDGE,"E61.MirrorCS");Q0=makeQuery(id+"F17.opChamfer","BLEND_EDGE",EDGE,{"blendedFrom":[makeQuery(id+"F12.opChamfer","BLEND_EDGE",EDGE,{"blendedFrom":[makeQuery(id+"F11.opExtrude","CAP_EDGE",EDGE,{"disambiguationData":[OSD([subQ0])],"isStart":false}),makeQuery(id+"F11.opExtrude","SWEPT_FACE",FACE,{"disambiguationData":[OSD([subQ0])]})],"blendedInto":[makeQuery(id+"F11.opExtrude","SWEPT_FACE",FACE,{"disambiguationData":[OSD([subQ0])]})]}),makeQuery(id+"F12.opChamfer","BLEND_FACE",FACE,{"disambiguationData":[OSD([subQ0])]})],"blendedInto":[makeQuery(id+"F12.opChamfer","BLEND_FACE",FACE,{"disambiguationData":[OSD([subQ0])]})]});}
            var Q1;
            {var subQ0=sQuery(id+"F10.wireOp",EDGE,"E59");Q1=makeQuery(id+"F17.opChamfer","BLEND_EDGE",EDGE,{"blendedFrom":[makeQuery(id+"F12.opChamfer","BLEND_EDGE",EDGE,{"blendedFrom":[makeQuery(id+"F11.opExtrude","CAP_EDGE",EDGE,{"disambiguationData":[OSD([subQ0])],"isStart":false}),makeQuery(id+"F11.opExtrude","SWEPT_FACE",FACE,{"disambiguationData":[OSD([subQ0])]})],"blendedInto":[makeQuery(id+"F11.opExtrude","SWEPT_FACE",FACE,{"disambiguationData":[OSD([subQ0])]})]}),makeQuery(id+"F12.opChamfer","BLEND_FACE",FACE,{"disambiguationData":[OSD([subQ0])]})],"blendedInto":[makeQuery(id+"F12.opChamfer","BLEND_FACE",FACE,{"disambiguationData":[OSD([subQ0])]})]});}
            var Q2;
            {var subQ0=sQuery(id+"F10.wireOp",EDGE,"E60.MirrorCS");Q2=makeQuery(id+"F17.opChamfer","BLEND_EDGE",EDGE,{"blendedFrom":[makeQuery(id+"F12.opChamfer","BLEND_EDGE",EDGE,{"blendedFrom":[makeQuery(id+"F11.opExtrude","CAP_EDGE",EDGE,{"disambiguationData":[OSD([subQ0])],"isStart":false}),makeQuery(id+"F11.opExtrude","SWEPT_FACE",FACE,{"disambiguationData":[OSD([subQ0])]})],"blendedInto":[makeQuery(id+"F11.opExtrude","SWEPT_FACE",FACE,{"disambiguationData":[OSD([subQ0])]})]}),makeQuery(id+"F12.opChamfer","BLEND_FACE",FACE,{"disambiguationData":[OSD([subQ0])]})],"blendedInto":[makeQuery(id+"F12.opChamfer","BLEND_FACE",FACE,{"disambiguationData":[OSD([subQ0])]})]});}
            var Q3;
            {var subQ0=sQuery(id+"F10.wireOp",EDGE,"E57");Q3=makeQuery(id+"F17.opChamfer","BLEND_EDGE",EDGE,{"blendedFrom":[makeQuery(id+"F12.opChamfer","BLEND_EDGE",EDGE,{"blendedFrom":[makeQuery(id+"F11.opExtrude","CAP_EDGE",EDGE,{"disambiguationData":[OSD([subQ0])],"isStart":false}),makeQuery(id+"F11.opExtrude","SWEPT_FACE",FACE,{"disambiguationData":[OSD([subQ0])]})],"blendedInto":[makeQuery(id+"F11.opExtrude","SWEPT_FACE",FACE,{"disambiguationData":[OSD([subQ0])]})]}),makeQuery(id+"F12.opChamfer","BLEND_FACE",FACE,{"disambiguationData":[OSD([subQ0])]})],"blendedInto":[makeQuery(id+"F12.opChamfer","BLEND_FACE",FACE,{"disambiguationData":[OSD([subQ0])]})]});}
            var Q4;
            {var subQ0=sQuery(id+"F10.wireOp",EDGE,"E59");Q4=makeQuery(id+"F17.opChamfer","BLEND_EDGE",EDGE,{"blendedFrom":[makeQuery(id+"F13.opChamfer","BLEND_EDGE",EDGE,{"blendedFrom":[makeQuery(id+"F11.opExtrude","CAP_EDGE",EDGE,{"disambiguationData":[OSD([subQ0])],"isStart":true}),makeQuery(id+"F11.opExtrude","SWEPT_FACE",FACE,{"disambiguationData":[OSD([subQ0])]})],"blendedInto":[makeQuery(id+"F11.opExtrude","SWEPT_FACE",FACE,{"disambiguationData":[OSD([subQ0])]})]}),makeQuery(id+"F13.opChamfer","BLEND_FACE",FACE,{"disambiguationData":[OSD([subQ0])]})],"blendedInto":[makeQuery(id+"F13.opChamfer","BLEND_FACE",FACE,{"disambiguationData":[OSD([subQ0])]})]});}
            var Q5;
            {var subQ0=sQuery(id+"F10.wireOp",EDGE,"E57");Q5=makeQuery(id+"F17.opChamfer","BLEND_EDGE",EDGE,{"blendedFrom":[makeQuery(id+"F13.opChamfer","BLEND_EDGE",EDGE,{"blendedFrom":[makeQuery(id+"F11.opExtrude","CAP_EDGE",EDGE,{"disambiguationData":[OSD([subQ0])],"isStart":true}),makeQuery(id+"F11.opExtrude","SWEPT_FACE",FACE,{"disambiguationData":[OSD([subQ0])]})],"blendedInto":[makeQuery(id+"F11.opExtrude","SWEPT_FACE",FACE,{"disambiguationData":[OSD([subQ0])]})]}),makeQuery(id+"F13.opChamfer","BLEND_FACE",FACE,{"disambiguationData":[OSD([subQ0])]})],"blendedInto":[makeQuery(id+"F13.opChamfer","BLEND_FACE",FACE,{"disambiguationData":[OSD([subQ0])]})]});}
            var Q6;
            {var subQ0=sQuery(id+"F10.wireOp",EDGE,"E60.MirrorCS");Q6=makeQuery(id+"F17.opChamfer","BLEND_EDGE",EDGE,{"blendedFrom":[makeQuery(id+"F13.opChamfer","BLEND_EDGE",EDGE,{"blendedFrom":[makeQuery(id+"F11.opExtrude","CAP_EDGE",EDGE,{"disambiguationData":[OSD([subQ0])],"isStart":true}),makeQuery(id+"F11.opExtrude","SWEPT_FACE",FACE,{"disambiguationData":[OSD([subQ0])]})],"blendedInto":[makeQuery(id+"F11.opExtrude","SWEPT_FACE",FACE,{"disambiguationData":[OSD([subQ0])]})]}),makeQuery(id+"F13.opChamfer","BLEND_FACE",FACE,{"disambiguationData":[OSD([subQ0])]})],"blendedInto":[makeQuery(id+"F13.opChamfer","BLEND_FACE",FACE,{"disambiguationData":[OSD([subQ0])]})]});}
            fillet(context, id + "F18", {"entities" : qUnion([Q0, Q1, Q2, Q3, Q4, Q5, Q6]), "radius" : 5.08 * mm, "tangentPropagation" : true, "allowEdgeOverflow" : false});
        }
    });
